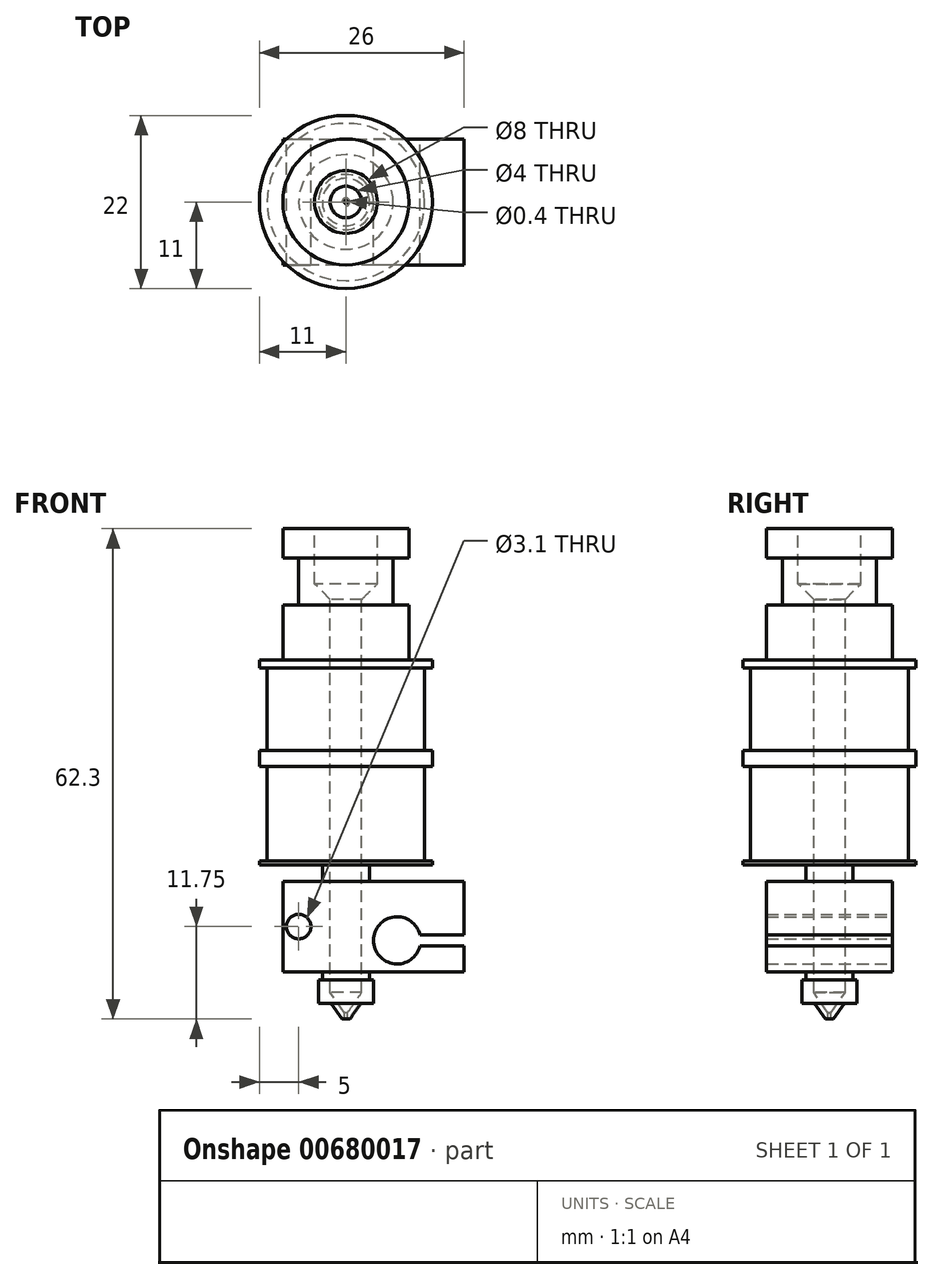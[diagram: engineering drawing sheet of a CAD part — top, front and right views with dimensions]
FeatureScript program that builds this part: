
annotation { "Feature Type Name" : "Feature", "Feature Type Description" : "" }
export const myFeature = defineFeature(function(context is Context, id is Id, definition is map)
    precondition{}
    {
        {
            var Q0;
            Q0=qCreatedBy(makeId("Front.planeOp"),FACE);
            var sketch = newSketch(context, id + "F0", { "sketchPlane" : qUnion([Q0])});
            skLineSegment(sketch, "E0", {"start": v(0, 0) * mm, "end": v(8, 0) * mm});
            skLineSegment(sketch, "E1", {"start": v(8, 0) * mm, "end": v(8, -3.7) * mm});
            skLineSegment(sketch, "E2", {"start": v(8, -3.7) * mm, "end": v(6, -3.7) * mm});
            skLineSegment(sketch, "E3", {"start": v(6, -3.7) * mm, "end": v(6, -9.7) * mm});
            skLineSegment(sketch, "E4", {"start": v(6, -9.7) * mm, "end": v(8, -9.7) * mm});
            skLineSegment(sketch, "E5", {"start": v(8, -9.7) * mm, "end": v(8, -16.7) * mm});
            skLineSegment(sketch, "E6", {"start": v(8, -16.7) * mm, "end": v(11, -16.7) * mm});
            skLineSegment(sketch, "E7", {"start": v(11, -16.7) * mm, "end": v(11, -17.7) * mm});
            skLineSegment(sketch, "E8", {"start": v(11, -17.7) * mm, "end": v(10, -17.7) * mm});
            skLineSegment(sketch, "E9", {"start": v(10, -17.7) * mm, "end": v(10, -28.2) * mm});
            skLineSegment(sketch, "E10", {"start": v(10, -28.2) * mm, "end": v(11, -28.2) * mm});
            skLineSegment(sketch, "E11", {"start": v(11, -28.2) * mm, "end": v(11, -30.2) * mm});
            skLineSegment(sketch, "E12", {"start": v(11, -30.2) * mm, "end": v(10, -30.2) * mm});
            skLineSegment(sketch, "E13", {"start": v(10, -30.2) * mm, "end": v(10, -42.2) * mm});
            skLineSegment(sketch, "E14", {"start": v(10, -42.2) * mm, "end": v(11, -42.2) * mm});
            skLineSegment(sketch, "E15", {"start": v(11, -42.2) * mm, "end": v(11, -42.7) * mm});
            skLineSegment(sketch, "E16", {"start": v(11, -42.7) * mm, "end": v(3, -42.7) * mm});
            skLineSegment(sketch, "E17", {"start": v(3, -57.3) * mm, "end": v(3.5, -57.3) * mm});
            skLineSegment(sketch, "E18", {"start": v(3.5, -57.3) * mm, "end": v(3.5, -60.3) * mm});
            skLineSegment(sketch, "E19", {"start": v(3.5, -60.3) * mm, "end": v(1.9, -60.3) * mm});
            skLineSegment(sketch, "E20", {"start": v(8, -9.7) * mm, "end": v(8, -3.7) * mm, "construction": true});
            skLineSegment(sketch, "E21", {"start": v(11, -17.7) * mm, "end": v(11, -28.2) * mm, "construction": true});
            skLineSegment(sketch, "E22", {"start": v(11, -30.2) * mm, "end": v(11, -42.2) * mm, "construction": true});
            skLineSegment(sketch, "E23", {"start": v(4, 0) * mm, "end": v(4, -7) * mm});
            skLineSegment(sketch, "E24", {"start": v(4, -7) * mm, "end": v(2, -9) * mm});
            skLineSegment(sketch, "E25", {"start": v(2, -9) * mm, "end": v(2, -58.93) * mm});
            skLineSegment(sketch, "E26", {"start": v(2, -58.93) * mm, "end": v(0.2, -61.5) * mm});
            skLineSegment(sketch, "E27", {"start": v(0.2, -61.5) * mm, "end": v(0.2, -62.3) * mm});
            skLineSegment(sketch, "E28", {"start": v(0.2, -62.3) * mm, "end": v(0.5, -62.3) * mm});
            skLineSegment(sketch, "E29", {"start": v(0.5, -62.3) * mm, "end": v(1.9, -60.3) * mm});
            skLineSegment(sketch, "E30", {"start": v(10, -28.2) * mm, "end": v(10, -30.2) * mm, "construction": true});
            skLineSegment(sketch, "E31", {"start": v(3, -42.7) * mm, "end": v(3, -49.8) * mm});
            skLineSegment(sketch, "E32", {"start": v(3, -49.8) * mm, "end": v(3, -57.3) * mm});
            skLineSegment(sketch, "E33", {"start": v(0, 0) * mm, "end": v(0, -84) * mm});
            skSolve(sketch);
        }
        {
            var Q0;
            {var subQ2=sQuery(id+"F0.wireOp",EDGE,"E1");Q0=makeQuery(id+"F0.imprint","IMPRINT",FACE,{"disambiguationData":[TD([[makeQuery(id+"F0.imprint","IMPRINT",EDGE,{"derivedFrom":subQ2}),-1.0]])]});}
            var Q1;
            Q1=sQuery(id+"F0.wireOp",EDGE,"E33");
            revolve(context, id + "F1", {"entities" : qUnion([Q0]), "axis" : qUnion([Q1]), "revolveType" : RevolveType.FULL});
        }
        {
            var Q0;
            Q0=qCreatedBy(makeId("Top.planeOp"),FACE);
            cPlane(context, id + "F2", {"entities" : qUnion([Q0]), "cplaneType" : CPlaneType.OFFSET, "offset" : 44.8 * mm, "oppositeDirection" : true, "width" : 150 * mm, "height" : 150 * mm});
        }
        {
            var Q0;
            Q0=qCreatedBy(id+"F2.planeOp",FACE);
            var sketch = newSketch(context, id + "F3", { "sketchPlane" : qUnion([Q0])});
            skCircle(sketch, "E34", {"center": v(0, 0) * mm, "radius": 3 * mm});
            skLineSegment(sketch, "E35", {"start": v(-8, 8) * mm, "end": v(15, 8) * mm});
            skLineSegment(sketch, "E36", {"start": v(15, 8) * mm, "end": v(15, -8) * mm});
            skLineSegment(sketch, "E37", {"start": v(15, -8) * mm, "end": v(-8, -8) * mm});
            skLineSegment(sketch, "E38", {"start": v(-8, -8) * mm, "end": v(-8, 8) * mm});
            skLineSegment(sketch, "E39", {"start": v(0, 0) * mm, "end": v(-8, 0) * mm, "construction": true});
            skSolve(sketch);
        }
        {
            var Q0;
            Q0=makeQuery(id+"F3.imprint","IMPRINT",FACE,{"disambiguationData":[TD([[makeQuery(id+"F3.imprint","IMPRINT",EDGE,{"derivedFrom":sQuery(id+"F3.wireOp",EDGE,"E34")}),-1.0]])]});
            extrude(context, id + "F4", {"entities" : qUnion([Q0]), "operationType" : NewBodyOperationType.ADD, "oppositeDirection" : true, "depth" : 11.5 * mm});
        }
        {
            var Q0;
            Q0=makeQuery(id+"F4.opExtrude","SWEPT_FACE",FACE,{"disambiguationData":[OSD([sQuery(id+"F3.wireOp",EDGE,"E35")])]});
            var sketch = newSketch(context, id + "F5", { "sketchPlane" : qUnion([Q0])});
            skLineSegment(sketch, "E40.0.0", {"start": v(8, -44.8) * mm, "end": v(-15, -44.8) * mm, "construction": true});
            skLineSegment(sketch, "E40.0.1", {"start": v(-15, -44.8) * mm, "end": v(-15, -56.3) * mm, "construction": true});
            skLineSegment(sketch, "E40.0.2", {"start": v(-15, -56.3) * mm, "end": v(8, -56.3) * mm, "construction": true});
            skLineSegment(sketch, "E40.0.3", {"start": v(8, -56.3) * mm, "end": v(8, -44.8) * mm, "construction": true});
            skCircle(sketch, "E41", {"center": v(-6.5, -52.3) * mm, "radius": 3 * mm});
            skCircle(sketch, "E42", {"center": v(6, -50.55) * mm, "radius": 1.55 * mm});
            skLineSegment(sketch, "E43", {"start": v(-9.42, -51.6) * mm, "end": v(-15, -51.6) * mm});
            skLineSegment(sketch, "E44", {"start": v(-15, -51.6) * mm, "end": v(-15, -53) * mm});
            skLineSegment(sketch, "E45", {"start": v(-15, -53) * mm, "end": v(-9.42, -53) * mm});
            skSolve(sketch);
        }
        {
            var Q0;
            Q0=qSketchRegion(id+"F5",true);
            extrude(context, id + "F6", {"entities" : qUnion([Q0]), "operationType" : NewBodyOperationType.REMOVE, "endBound" : BoundingType.THROUGH_ALL, "oppositeDirection" : true, "depth" : 25 * mm});
        }
    });
